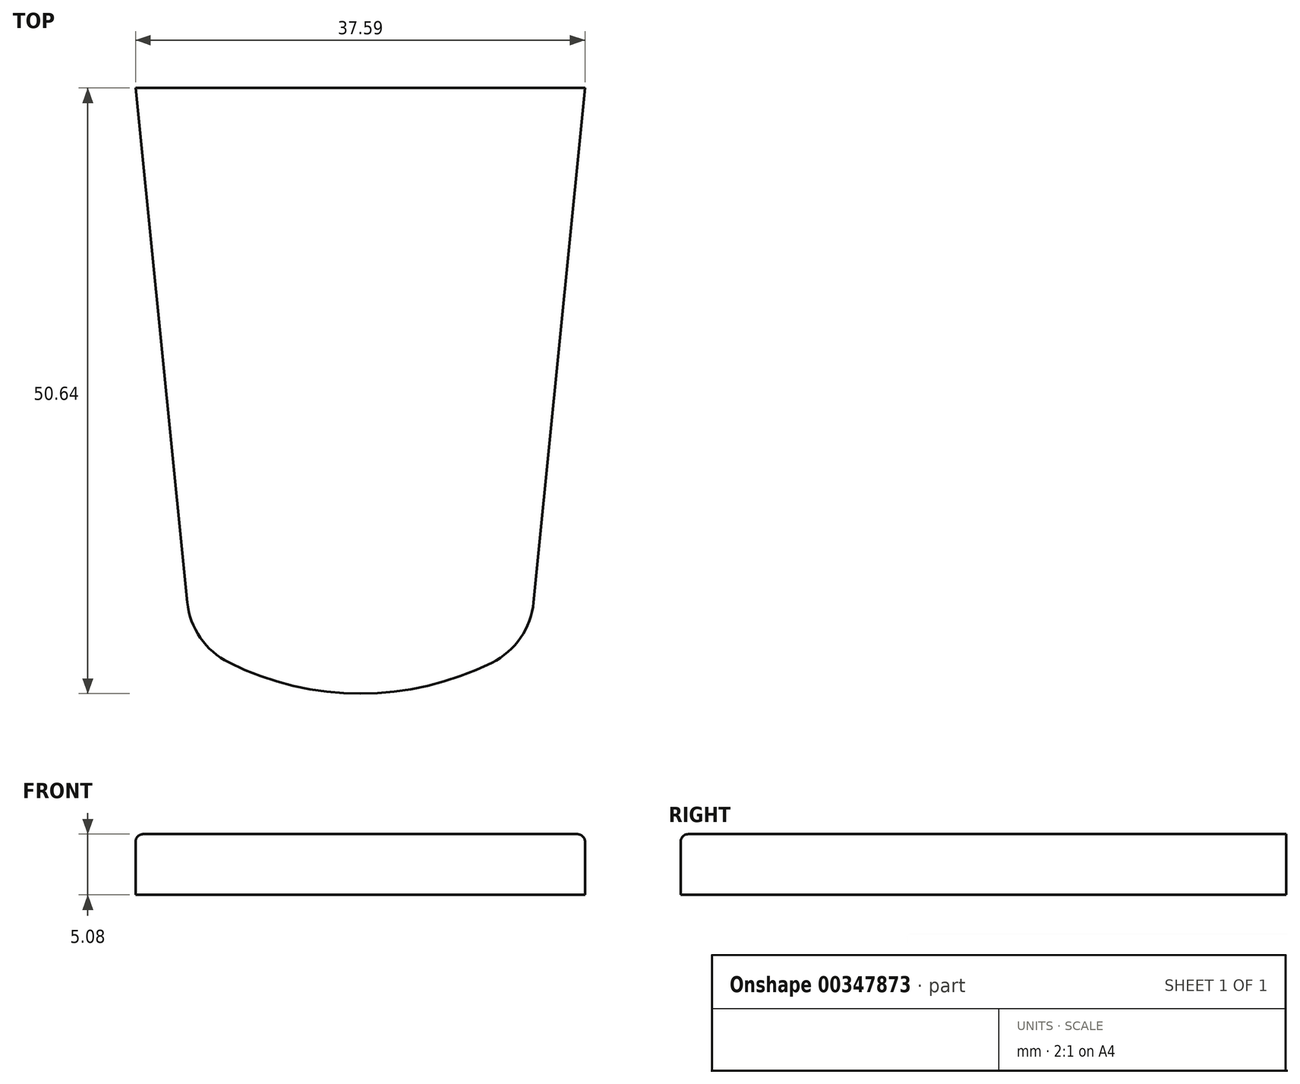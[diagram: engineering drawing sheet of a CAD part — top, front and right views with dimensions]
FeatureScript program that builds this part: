
annotation { "Feature Type Name" : "Feature", "Feature Type Description" : "" }
export const myFeature = defineFeature(function(context is Context, id is Id, definition is map)
    precondition{}
    {
        {
            var Q0;
            Q0=qCreatedBy(makeId("Top.planeOp"),FACE);
            var sketch = newSketch(context, id + "F0", { "sketchPlane" : qUnion([Q0])});
            skLineSegment(sketch, "E0", {"start": v(4.33, 7.8) * mm, "end": v(0, 50.8) * mm});
            skLineSegment(sketch, "E1", {"start": v(37.6, 50.8) * mm, "end": v(33.3, 7.8) * mm});
            skArc(sketch, "E2", {"start": v(7.8, 2.76) * mm, "mid": v(18.8, 0.16) * mm, "end": v(29.8, 2.75) * mm});
            skPoint(sketch, "E3.visualSharp", {"position": v(32.98, 4.64) * mm});
            skArc(sketch, "E3.filletArc", {"start": v(29.8, 2.75) * mm, "mid": v(32.2, 4.83) * mm, "end": v(33.3, 7.8) * mm});
            skPoint(sketch, "E4.visualSharp", {"position": v(4.64, 4.65) * mm});
            skArc(sketch, "E4.filletArc", {"start": v(4.33, 7.8) * mm, "mid": v(5.42, 4.83) * mm, "end": v(7.8, 2.76) * mm});
            skLineSegment(sketch, "E5", {"start": v(0, 50.8) * mm, "end": v(37.6, 50.8) * mm});
            skSolve(sketch);
        }
        {
            var Q0;
            Q0=makeQuery(id+"F0.imprint","IMPRINT",FACE,{"disambiguationData":[TD([[makeQuery(id+"F0.imprint","IMPRINT",EDGE,{"derivedFrom":sQuery(id+"F0.wireOp",EDGE,"E0")}),-1.0]])]});
            extrude(context, id + "F1", {"entities" : qUnion([Q0]), "depth" : 5.08 * mm});
        }
        {
            var Q0;
            Q0=makeQuery(id+"F1.opExtrude","CAP_EDGE",EDGE,{"disambiguationData":[OSD([sQuery(id+"F0.wireOp",EDGE,"E2")])],"isStart":false});
            var Q1;
            Q1=makeQuery(id+"F1.opExtrude","CAP_EDGE",EDGE,{"disambiguationData":[OSD([sQuery(id+"F0.wireOp",EDGE,"E3.filletArc")])],"isStart":false});
            var Q2;
            Q2=makeQuery(id+"F1.opExtrude","CAP_EDGE",EDGE,{"disambiguationData":[OSD([sQuery(id+"F0.wireOp",EDGE,"UiAhYkmi-7jta-T0Or-lWjq-xMjNalCsZch8")])],"isStart":false});
            var Q3;
            Q3=makeQuery(id+"F1.opExtrude","CAP_EDGE",EDGE,{"disambiguationData":[OSD([sQuery(id+"F0.wireOp",EDGE,"B8bHT2ps-UukG-Pm2Y-rBD1-e014lnROOPxp")])],"isStart":false});
            var Q4;
            Q4=makeQuery(id+"F1.opExtrude","CAP_EDGE",EDGE,{"disambiguationData":[OSD([sQuery(id+"F0.wireOp",EDGE,"E1")])],"isStart":false});
            var Q5;
            Q5=makeQuery(id+"F1.opExtrude","CAP_EDGE",EDGE,{"disambiguationData":[OSD([sQuery(id+"F0.wireOp",EDGE,"E0")])],"isStart":false});
            var Q6;
            Q6=makeQuery(id+"F1.opExtrude","CAP_EDGE",EDGE,{"disambiguationData":[OSD([sQuery(id+"F0.wireOp",EDGE,"Rtt68xH8-7yW4-zRS4-VA9m-AwV4pYRkD65s")])],"isStart":false});
            var Q7;
            Q7=makeQuery(id+"F1.opExtrude","CAP_EDGE",EDGE,{"disambiguationData":[OSD([sQuery(id+"F0.wireOp",EDGE,"UdNmkYaI-UF4b-JsBr-dvE7-zJRFfNl67YsT")])],"isStart":false});
            var Q8;
            Q8=makeQuery(id+"F1.opExtrude","CAP_EDGE",EDGE,{"disambiguationData":[OSD([sQuery(id+"F0.wireOp",EDGE,"E4.filletArc")])],"isStart":false});
            var Q9;
            Q9=makeQuery(id+"F1.opExtrude","CAP_EDGE",EDGE,{"disambiguationData":[OSD([sQuery(id+"F0.wireOp",EDGE,"RhSqrOeS-0TPe-pkCG-VGfM-88bAThmU0TzT")])],"isStart":false});
            fillet(context, id + "F2", {"entities" : qUnion([Q0, Q1, Q2, Q3, Q4, Q5, Q6, Q7, Q8, Q9]), "radius" : 0.64 * mm, "tangentPropagation" : true, "allowEdgeOverflow" : false});
        }
    });
